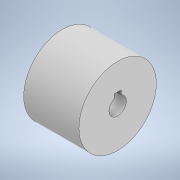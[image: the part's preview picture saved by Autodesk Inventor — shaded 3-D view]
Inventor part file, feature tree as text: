
AUTODESK INVENTOR PART (.ipt)
format: ipt  version: 2021.2 (Build 252289000, 289)  size: 110,080 bytes
history: native  units: in
note: dims shown in document units (in); Inventor stores cm internally (conversion verified against a paired STEP export)
features: sketch x2, revolve x1, extrude x1
ambient origin geometry x8: Origin, YZ Plane, XZ Plane, XY Plane, X Axis, Y Axis, Z Axis, Center Point
bodies: Solid1 (feature_tree)
feature tree (4):
  revolve  "Revolution1"  [1 undecoded]
  extrude  "Extrusion1"  TaperAngle=90.0deg  [1 undecoded]
  sketch  "Sketch1"  dims[d0=0.7in d1=1.0in]
  sketch  "Sketch2"  dims[d2=0.1575in d3=90.0deg d4=0.125in d5=0.125in d6=0.0in d7=0.0in]
note: 2 required parameter values undecoded (feature->parameter linkage not recoverable at this tier; creation-order binding heuristic only, values carry confidence <= 0.55)